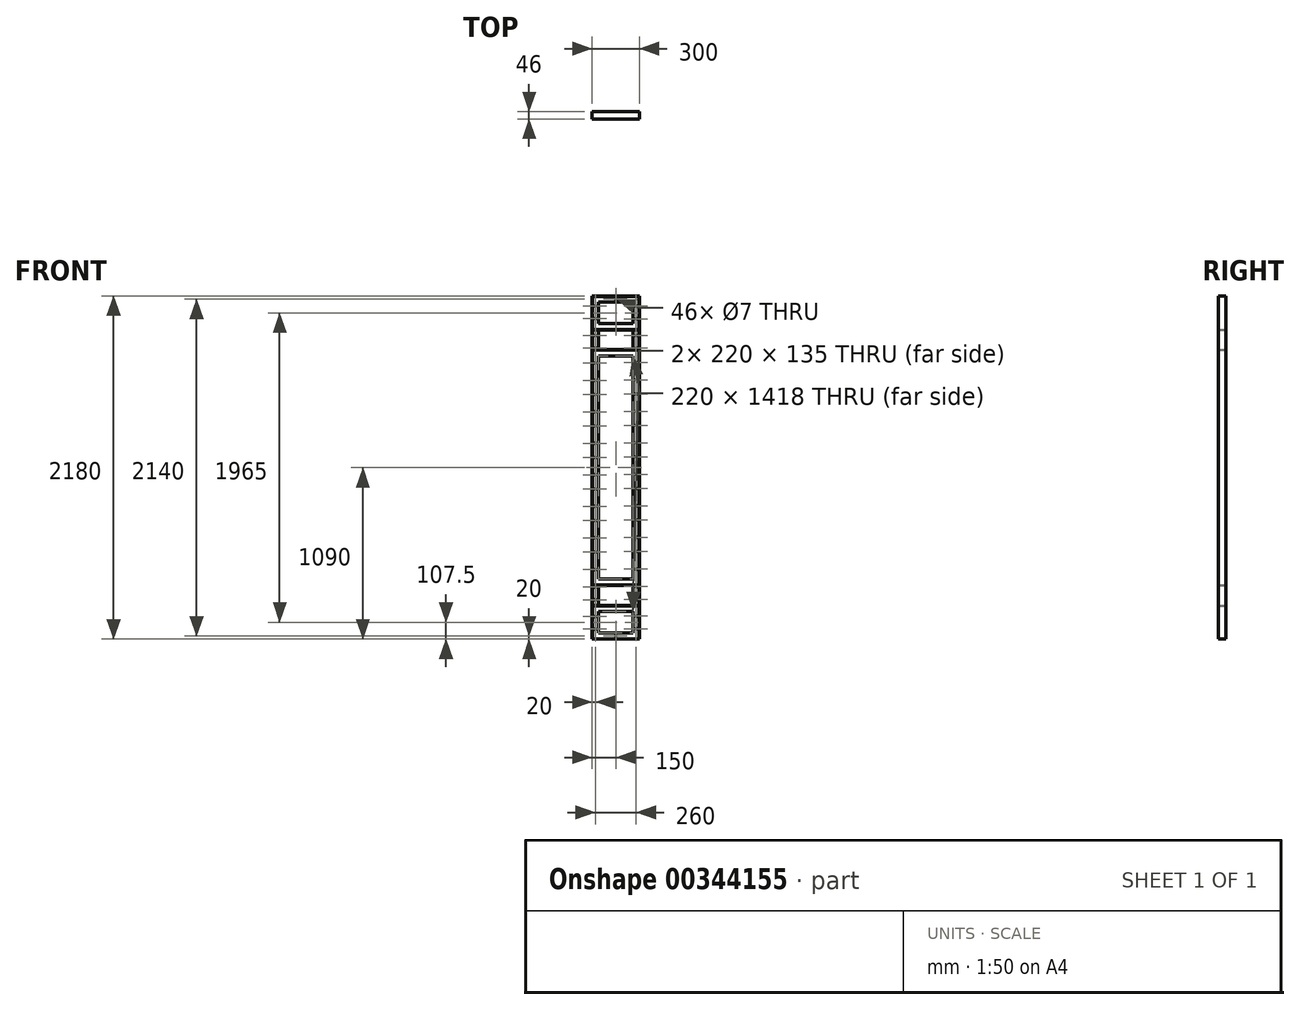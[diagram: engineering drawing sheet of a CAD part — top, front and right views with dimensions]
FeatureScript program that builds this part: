
annotation { "Feature Type Name" : "Feature", "Feature Type Description" : "" }
export const myFeature = defineFeature(function(context is Context, id is Id, definition is map)
    precondition{}
    {
        {
            var Q0;
            Q0=qCreatedBy(makeId("Front.planeOp"),FACE);
            var sketch = newSketch(context, id + "F0", { "sketchPlane" : qUnion([Q0])});
            skLineSegment(sketch, "E0.bottom", {"start": v(-150, 1090) * mm, "end": v(150, 1090) * mm});
            skLineSegment(sketch, "E0.top", {"start": v(-150, -1090) * mm, "end": v(150, -1090) * mm});
            skLineSegment(sketch, "E0.left", {"start": v(-150, 1090) * mm, "end": v(-150, -1090) * mm});
            skLineSegment(sketch, "E0.right", {"start": v(150, 1090) * mm, "end": v(150, -1090) * mm});
            skPoint(sketch, "E0.middle", {"position": v(0, 0) * mm});
            skLineSegment(sketch, "E1.bottom", {"start": v(-147, 1087) * mm, "end": v(147, 1087) * mm});
            skLineSegment(sketch, "E1.top", {"start": v(-147, -1087) * mm, "end": v(147, -1087) * mm});
            skLineSegment(sketch, "E1.left", {"start": v(-147, 1087) * mm, "end": v(-147, -1087) * mm});
            skLineSegment(sketch, "E1.right", {"start": v(147, 1087) * mm, "end": v(147, -1087) * mm});
            skLineSegment(sketch, "E2.bottom", {"start": v(-110, 1050) * mm, "end": v(110, 1050) * mm});
            skLineSegment(sketch, "E2.top", {"start": v(-110, 915) * mm, "end": v(110, 915) * mm});
            skLineSegment(sketch, "E2.left", {"start": v(-110, 1050) * mm, "end": v(-110, 915) * mm});
            skLineSegment(sketch, "E2.right", {"start": v(110, 1050) * mm, "end": v(110, 915) * mm});
            skPoint(sketch, "E2.middle", {"position": v(0, 982.5) * mm});
            skLineSegment(sketch, "E3", {"start": v(-147, 875) * mm, "end": v(147, 875) * mm});
            skLineSegment(sketch, "E4", {"start": v(-147, 878) * mm, "end": v(147, 878) * mm});
            skLineSegment(sketch, "E5", {"start": v(-147, 746) * mm, "end": v(147, 746) * mm});
            skLineSegment(sketch, "E6", {"start": v(-147, 749) * mm, "end": v(147, 749) * mm});
            skLineSegment(sketch, "E7", {"start": v(-110, 875) * mm, "end": v(-110, 749) * mm});
            skLineSegment(sketch, "E8", {"start": v(110, 875) * mm, "end": v(110, 749) * mm});
            skLineSegment(sketch, "E9.bottom", {"start": v(-110, 709) * mm, "end": v(110, 709) * mm});
            skLineSegment(sketch, "E9.top", {"start": v(-110, -709) * mm, "end": v(110, -709) * mm});
            skLineSegment(sketch, "E9.left", {"start": v(-110, 709) * mm, "end": v(-110, -709) * mm});
            skLineSegment(sketch, "E9.right", {"start": v(110, 709) * mm, "end": v(110, -709) * mm});
            skLineSegment(sketch, "E10.bottom", {"start": v(-110, -915) * mm, "end": v(110, -915) * mm});
            skLineSegment(sketch, "E10.top", {"start": v(-110, -1050) * mm, "end": v(110, -1050) * mm});
            skLineSegment(sketch, "E10.left", {"start": v(-110, -915) * mm, "end": v(-110, -1050) * mm});
            skLineSegment(sketch, "E10.right", {"start": v(110, -915) * mm, "end": v(110, -1050) * mm});
            skPoint(sketch, "E10.middle", {"position": v(0, -982.5) * mm});
            skPoint(sketch, "E10.middle.positionSnap0", {"position": v(0, -1087) * mm});
            skPoint(sketch, "E10.centerSnap0", {"position": v(0, -1087) * mm});
            skLineSegment(sketch, "E11", {"start": v(-147, -875) * mm, "end": v(147, -875) * mm});
            skLineSegment(sketch, "E12", {"start": v(-147, -878) * mm, "end": v(147, -878) * mm});
            skLineSegment(sketch, "E13", {"start": v(-147, -746) * mm, "end": v(147, -746) * mm});
            skLineSegment(sketch, "E14", {"start": v(-147, -749) * mm, "end": v(147, -749) * mm});
            skLineSegment(sketch, "E15", {"start": v(-110, -875) * mm, "end": v(-110, -749) * mm});
            skLineSegment(sketch, "E16", {"start": v(110, -749) * mm, "end": v(110, -875) * mm});
            skCircle(sketch, "E17", {"center": v(0, 1070) * mm, "radius": 3.5 * mm});
            skPoint(sketch, "E17.centerSnap0", {"position": v(0, 1087) * mm});
            skCircle(sketch, "E18", {"center": v(130, 1025) * mm, "radius": 3.5 * mm});
            skCircle(sketch, "E19", {"center": v(130, 945) * mm, "radius": 3.5 * mm});
            skCircle(sketch, "E20", {"center": v(130, 838) * mm, "radius": 3.5 * mm});
            skCircle(sketch, "E21", {"center": v(130, 758) * mm, "radius": 3.5 * mm});
            skCircle(sketch, "E22", {"center": v(130, 667) * mm, "radius": 3.5 * mm});
            skCircle(sketch, "E23", {"center": v(130, 557) * mm, "radius": 3.5 * mm});
            skCircle(sketch, "E24", {"center": v(130, 467) * mm, "radius": 3.5 * mm});
            skCircle(sketch, "E25", {"center": v(130, 357) * mm, "radius": 3.5 * mm});
            skCircle(sketch, "E26", {"center": v(130, 267) * mm, "radius": 3.5 * mm});
            skCircle(sketch, "E27", {"center": v(130, 157) * mm, "radius": 3.5 * mm});
            skCircle(sketch, "E28", {"center": v(130, 67) * mm, "radius": 3.5 * mm});
            skCircle(sketch, "E29", {"center": v(130, -43) * mm, "radius": 3.5 * mm});
            skCircle(sketch, "E30", {"center": v(130, -133) * mm, "radius": 3.5 * mm});
            skCircle(sketch, "E31", {"center": v(130, -243) * mm, "radius": 3.5 * mm});
            skCircle(sketch, "E32", {"center": v(130, -333) * mm, "radius": 3.5 * mm});
            skCircle(sketch, "E33", {"center": v(130, -443) * mm, "radius": 3.5 * mm});
            skCircle(sketch, "E34", {"center": v(130, -533) * mm, "radius": 3.5 * mm});
            skCircle(sketch, "E35", {"center": v(130, -645) * mm, "radius": 3.5 * mm});
            skCircle(sketch, "E36.MirrorC", {"center": v(-130, 664) * mm, "radius": 3.5 * mm});
            skCircle(sketch, "E37.MirrorC", {"center": v(-130, 759) * mm, "radius": 3.5 * mm});
            skCircle(sketch, "E38.MirrorC", {"center": v(-130, 839) * mm, "radius": 3.5 * mm});
            skCircle(sketch, "E39.MirrorC", {"center": v(-130, 946) * mm, "radius": 3.5 * mm});
            skCircle(sketch, "E40.MirrorC", {"center": v(-130, 1026) * mm, "radius": 3.5 * mm});
            skCircle(sketch, "E41.MirrorC", {"center": v(-130, 554) * mm, "radius": 3.5 * mm});
            skCircle(sketch, "E42.MirrorC", {"center": v(-130, 464) * mm, "radius": 3.5 * mm});
            skCircle(sketch, "E43.MirrorC", {"center": v(-130, 354) * mm, "radius": 3.5 * mm});
            skCircle(sketch, "E44.MirrorC", {"center": v(-130, 264) * mm, "radius": 3.5 * mm});
            skCircle(sketch, "E45.MirrorC", {"center": v(-130, 154) * mm, "radius": 3.5 * mm});
            skCircle(sketch, "E46.MirrorC", {"center": v(-130, 64) * mm, "radius": 3.5 * mm});
            skCircle(sketch, "E47.MirrorC", {"center": v(-130, -46) * mm, "radius": 3.5 * mm});
            skCircle(sketch, "E48.MirrorC", {"center": v(-130, -136) * mm, "radius": 3.5 * mm});
            skCircle(sketch, "E49.MirrorC", {"center": v(-130, -246) * mm, "radius": 3.5 * mm});
            skCircle(sketch, "E50.MirrorC", {"center": v(-130, -336) * mm, "radius": 3.5 * mm});
            skCircle(sketch, "E51.MirrorC", {"center": v(-130, -446) * mm, "radius": 3.5 * mm});
            skCircle(sketch, "E52.MirrorC", {"center": v(-130, -536) * mm, "radius": 3.5 * mm});
            skCircle(sketch, "E53.MirrorC", {"center": v(-130, -648) * mm, "radius": 3.5 * mm});
            skCircle(sketch, "E54", {"center": v(130, -756.5) * mm, "radius": 3.5 * mm});
            skCircle(sketch, "E55", {"center": v(130, -836.5) * mm, "radius": 3.5 * mm});
            skCircle(sketch, "E56", {"center": v(130, -943.5) * mm, "radius": 3.5 * mm});
            skCircle(sketch, "E57", {"center": v(130, -1023.5) * mm, "radius": 3.5 * mm});
            skCircle(sketch, "E58", {"center": v(0, -1070) * mm, "radius": 3.5 * mm});
            skCircle(sketch, "E59.MirrorC", {"center": v(-130, -759.5) * mm, "radius": 3.5 * mm});
            skCircle(sketch, "E60.MirrorC", {"center": v(-130, -839.5) * mm, "radius": 3.5 * mm});
            skCircle(sketch, "E61.MirrorC", {"center": v(-130, -946.5) * mm, "radius": 3.5 * mm});
            skCircle(sketch, "E62.MirrorC", {"center": v(-130, -1026.5) * mm, "radius": 3.5 * mm});
            skSolve(sketch);
        }
        {
            var Q0;
            Q0 = qSketchRegion(id + "F0", true);
            var Q1;
            {var subQ0=sQuery(id+"F0.wireOp",EDGE,"E13");Q1=makeQuery(id+"F0.imprint","IMPRINT",FACE,{"disambiguationData":[TD([[makeQuery(id+"F0.imprint","IMPRINT",EDGE,{"derivedFrom":subQ0}),-1.0]])]});}
            var Q2;
            {var subQ4=sQuery(id+"F0.wireOp",EDGE,"E12");Q2=makeQuery(id+"F0.imprint","IMPRINT",FACE,{"disambiguationData":[TD([[makeQuery(id+"F0.imprint","IMPRINT",EDGE,{"derivedFrom":subQ4}),1.0]])]});}
            var Q3;
            {var subQ0=sQuery(id+"F0.wireOp",EDGE,"E5");Q3=makeQuery(id+"F0.imprint","IMPRINT",FACE,{"disambiguationData":[TD([[makeQuery(id+"F0.imprint","IMPRINT",EDGE,{"derivedFrom":subQ0}),1.0]])]});}
            var Q4;
            {var subQ5=sQuery(id+"F0.wireOp",EDGE,"E4");Q4=makeQuery(id+"F0.imprint","IMPRINT",FACE,{"disambiguationData":[TD([[makeQuery(id+"F0.imprint","IMPRINT",EDGE,{"derivedFrom":subQ5}),-1.0]])]});}
            extrude(context, id + "F1", {"entities" : qUnion([Q0, Q1, Q2, Q3, Q4]), "depth" : 46 * mm});
        }
        {
            var Q0;
            {var subQ1=sQuery(id+"F0.wireOp",EDGE,"E1.bottom");Q0=makeQuery(id+"F0.imprint","IMPRINT",FACE,{"disambiguationData":[TD([[makeQuery(id+"F0.imprint","IMPRINT",EDGE,{"derivedFrom":subQ1}),-1.0]])]});}
            var Q1;
            {var subQ5=sQuery(id+"F0.wireOp",EDGE,"E7");Q1=makeQuery(id+"F0.imprint","IMPRINT",FACE,{"disambiguationData":[TD([[makeQuery(id+"F0.imprint","IMPRINT",EDGE,{"derivedFrom":subQ5}),-1.0]])]});}
            var Q2;
            {var subQ5=sQuery(id+"F0.wireOp",EDGE,"E8");Q2=makeQuery(id+"F0.imprint","IMPRINT",FACE,{"disambiguationData":[TD([[makeQuery(id+"F0.imprint","IMPRINT",EDGE,{"derivedFrom":subQ5}),1.0]])]});}
            var Q3;
            {var subQ0=sQuery(id+"F0.wireOp",EDGE,"E5");Q3=makeQuery(id+"F0.imprint","IMPRINT",FACE,{"disambiguationData":[TD([[makeQuery(id+"F0.imprint","IMPRINT",EDGE,{"derivedFrom":subQ0}),-1.0]])]});}
            var Q4;
            {var subQ5=sQuery(id+"F0.wireOp",EDGE,"E15");Q4=makeQuery(id+"F0.imprint","IMPRINT",FACE,{"disambiguationData":[TD([[makeQuery(id+"F0.imprint","IMPRINT",EDGE,{"derivedFrom":subQ5}),1.0]])]});}
            var Q5;
            {var subQ5=sQuery(id+"F0.wireOp",EDGE,"E16");Q5=makeQuery(id+"F0.imprint","IMPRINT",FACE,{"disambiguationData":[TD([[makeQuery(id+"F0.imprint","IMPRINT",EDGE,{"derivedFrom":subQ5}),1.0]])]});}
            var Q6;
            {var subQ1=sQuery(id+"F0.wireOp",EDGE,"E1.top");Q6=makeQuery(id+"F0.imprint","IMPRINT",FACE,{"disambiguationData":[TD([[makeQuery(id+"F0.imprint","IMPRINT",EDGE,{"derivedFrom":subQ1}),1.0]])]});}
            extrude(context, id + "F2", {"entities" : qUnion([Q0, Q1, Q2, Q3, Q4, Q5, Q6]), "operationType" : NewBodyOperationType.ADD, "depth" : 3 * mm});
        }
    });
